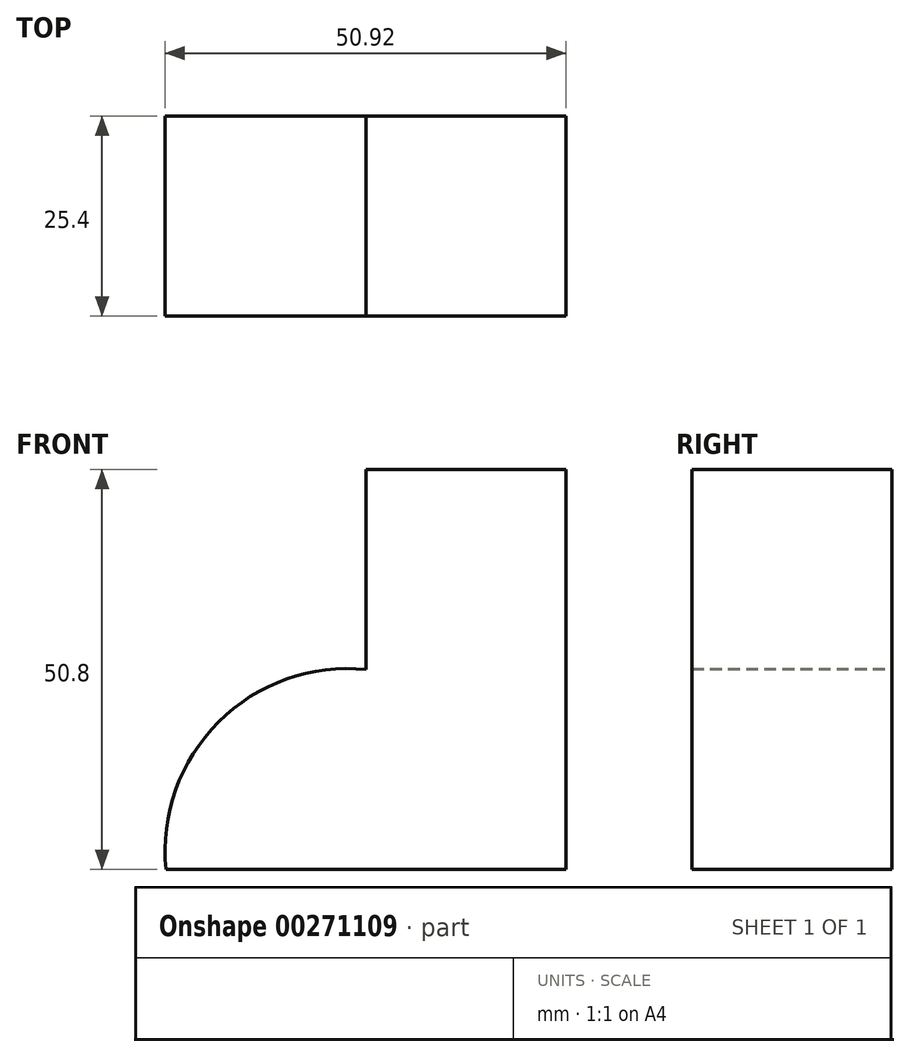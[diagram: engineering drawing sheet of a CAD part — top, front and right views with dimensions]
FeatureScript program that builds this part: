
annotation { "Feature Type Name" : "Feature", "Feature Type Description" : "" }
export const myFeature = defineFeature(function(context is Context, id is Id, definition is map)
    precondition{}
    {
        {
            var Q0;
            Q0=qCreatedBy(makeId("Front.planeOp"),FACE);
            var sketch = newSketch(context, id + "F0", { "sketchPlane" : qUnion([Q0])});
            skLineSegment(sketch, "E0", {"start": v(0, 0) * mm, "end": v(-50.8, 0) * mm});
            skLineSegment(sketch, "E1", {"start": v(0, 0) * mm, "end": v(0, 50.8) * mm});
            skLineSegment(sketch, "E2", {"start": v(0, 50.8) * mm, "end": v(-25.4, 50.8) * mm});
            skLineSegment(sketch, "E3", {"start": v(-25.4, 50.8) * mm, "end": v(-25.4, 25.4) * mm});
            skArc(sketch, "E4", {"start": v(-25.4, 25.4) * mm, "mid": v(-44.13, 18.73) * mm, "end": v(-50.8, 0) * mm});
            skSolve(sketch);
        }
        {
            var Q0;
            Q0=makeQuery(id+"F0.imprint","IMPRINT",FACE,{"disambiguationData":[TD([[makeQuery(id+"F0.imprint","IMPRINT",EDGE,{"derivedFrom":sQuery(id+"F0.wireOp",EDGE,"E0")}),-1.0]])]});
            extrude(context, id + "F1", {"entities" : qUnion([Q0]), "depth" : 25.4 * mm});
        }
    });
